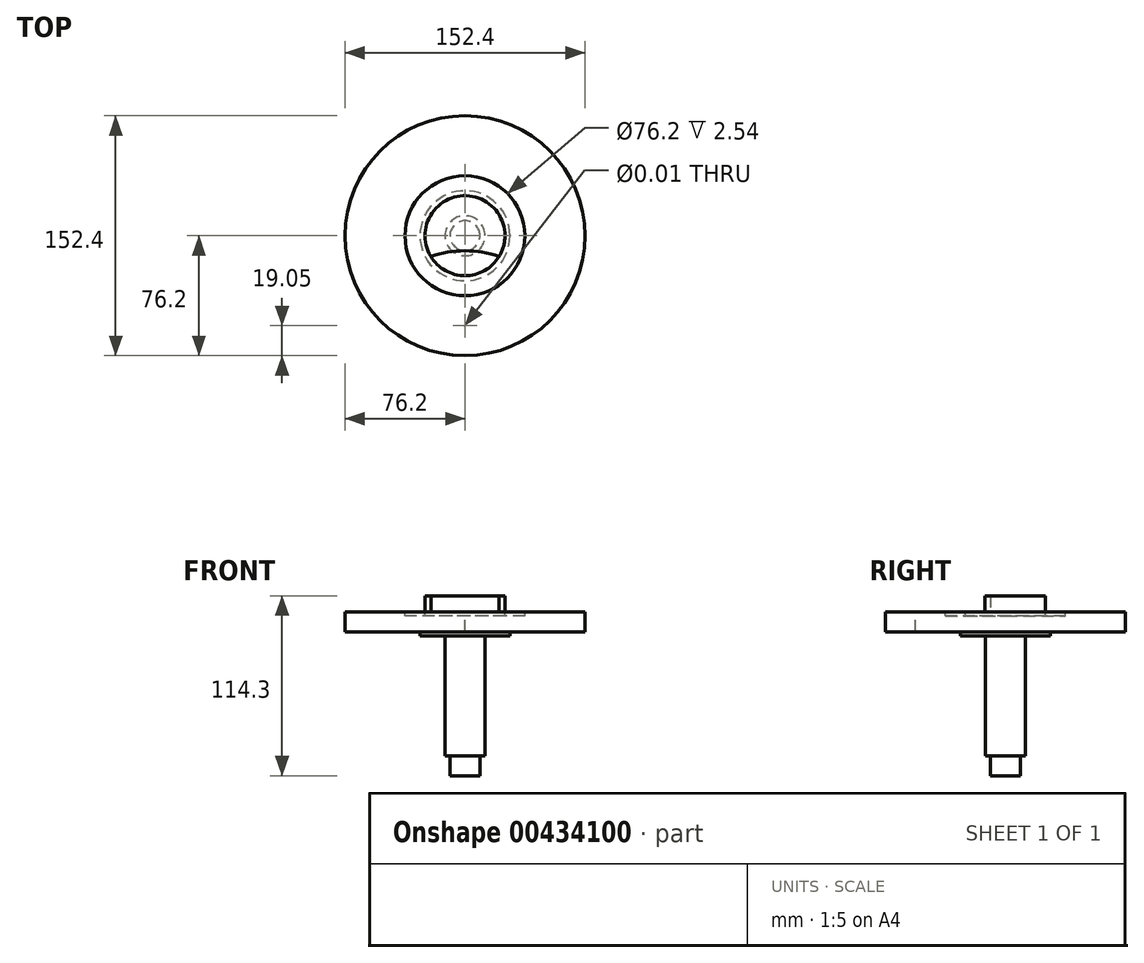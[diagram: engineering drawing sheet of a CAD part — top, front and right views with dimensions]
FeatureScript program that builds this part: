
annotation { "Feature Type Name" : "Feature", "Feature Type Description" : "" }
export const myFeature = defineFeature(function(context is Context, id is Id, definition is map)
    precondition{}
    {
        {
            var Q0;
            Q0=qCreatedBy(makeId("Front.planeOp"),FACE);
            var sketch = newSketch(context, id + "F0", { "sketchPlane" : qUnion([Q0])});
            skLineSegment(sketch, "E0", {"start": v(0, 0) * mm, "end": v(-25.4, 0) * mm});
            skLineSegment(sketch, "E1", {"start": v(-25.4, 0) * mm, "end": v(-25.4, -12.7) * mm});
            skLineSegment(sketch, "E2", {"start": v(-25.4, -12.7) * mm, "end": v(-38.1, -12.7) * mm});
            skLineSegment(sketch, "E3", {"start": v(-38.1, -12.7) * mm, "end": v(-38.1, -10.16) * mm});
            skLineSegment(sketch, "E4", {"start": v(-38.1, -10.16) * mm, "end": v(-76.2, -10.16) * mm});
            skLineSegment(sketch, "E5", {"start": v(-76.2, -10.16) * mm, "end": v(-76.2, -22.86) * mm});
            skLineSegment(sketch, "E6", {"start": v(-76.2, -22.86) * mm, "end": v(-28.58, -22.86) * mm});
            skLineSegment(sketch, "E7", {"start": v(-12.7, -25.4) * mm, "end": v(-12.7, -101.6) * mm});
            skLineSegment(sketch, "E8", {"start": v(-12.7, -101.6) * mm, "end": v(-9.52, -101.6) * mm});
            skLineSegment(sketch, "E9", {"start": v(-9.52, -101.6) * mm, "end": v(-9.52, -114.3) * mm});
            skLineSegment(sketch, "E10", {"start": v(-9.52, -114.3) * mm, "end": v(0, -114.3) * mm});
            skLineSegment(sketch, "E11", {"start": v(0, -114.3) * mm, "end": v(0, 0) * mm});
            skLineSegment(sketch, "E12", {"start": v(-28.58, -22.86) * mm, "end": v(-28.58, -25.4) * mm});
            skLineSegment(sketch, "E13", {"start": v(-28.58, -25.4) * mm, "end": v(-12.7, -25.4) * mm});
            skLineSegment(sketch, "E14", {"start": v(0, 17.27) * mm, "end": v(0, -123.9) * mm, "construction": true});
            skSolve(sketch);
        }
        {
            var Q0;
            Q0=makeQuery(id+"F0.imprint","IMPRINT",FACE,{"disambiguationData":[TD([[makeQuery(id+"F0.imprint","IMPRINT",EDGE,{"derivedFrom":sQuery(id+"F0.wireOp",EDGE,"E0")}),1.0]])]});
            var Q1;
            Q1=sQuery(id+"F0.wireOp",EDGE,"E14");
            var Q2;
            Q2=sQuery(id+"F0.wireOp",EDGE,"E11");
            var Q3;
            Q3=sQuery(id+"F0.wireOp",EDGE,"E0");
            var Q4;
            Q4=sQuery(id+"F0.wireOp",EDGE,"E1");
            var Q5;
            Q5=sQuery(id+"F0.wireOp",EDGE,"E2");
            var Q6;
            Q6=sQuery(id+"F0.wireOp",EDGE,"E3");
            var Q7;
            Q7=sQuery(id+"F0.wireOp",EDGE,"E4");
            var Q8;
            Q8=sQuery(id+"F0.wireOp",EDGE,"E5");
            var Q9;
            Q9=sQuery(id+"F0.wireOp",EDGE,"E6");
            var Q10;
            Q10=sQuery(id+"F0.wireOp",EDGE,"E12");
            var Q11;
            Q11=sQuery(id+"F0.wireOp",EDGE,"E13");
            var Q12;
            Q12=sQuery(id+"F0.wireOp",EDGE,"E7");
            var Q13;
            Q13=sQuery(id+"F0.wireOp",EDGE,"E8");
            var Q14;
            Q14=sQuery(id+"F0.wireOp",EDGE,"E9");
            var Q15;
            Q15=sQuery(id+"F0.wireOp",EDGE,"E10");
            var Q16;
            Q16=sQuery(id+"F0.wireOp",EDGE,"E14");
            revolve(context, id + "F1", {"entities" : qUnion([Q0]), "surfaceEntities" : qUnion([Q1, Q2, Q3, Q4, Q5, Q6, Q7, Q8, Q9, Q10, Q11, Q12, Q13, Q14, Q15]), "axis" : qUnion([Q16]), "revolveType" : RevolveType.FULL});
        }
        {
            var Q0;
            Q0=makeQuery(id+"F1.opRevolve","SWEPT_FACE",FACE,{"disambiguationData":[OSD([sQuery(id+"F0.wireOp",EDGE,"E4")])]});
            var sketch = newSketch(context, id + "F2", { "sketchPlane" : qUnion([Q0])});
            skCircle(sketch, "E15", {"center": v(0, -76.2) * mm, "radius": 66.68 * mm});
            skSolve(sketch);
        }
        {
            var Q0;
            {var subQ0=sQuery(id+"F2.wireOp",EDGE,"E15");var subQ1=makeQuery(id+"F1.opRevolve","SWEPT_EDGE",EDGE,{"disambiguationData":[OSD([sQuery(id+"F0.wireOp",EDGE,"E3"),sQuery(id+"F0.wireOp",EDGE,"E4")])]});var subQ2=makeQuery(id+"F2.imprint","INTERSECT",VERTEX,{"disambiguationData":[OD(0.0)],"derivedFrom":[subQ1,subQ0]});Q0=makeQuery(id+"F2.imprint","IMPRINT",FACE,{"disambiguationData":[TD([[makeQuery(id+"F2.imprint","IMPRINT",EDGE,{"disambiguationData":[TD([[subQ2,-1.0]])],"derivedFrom":subQ0}),1.0]])]});}
            extrude(context, id + "F3", {"entities" : qUnion([Q0]), "operationType" : NewBodyOperationType.REMOVE, "depth" : 25.4 * mm});
        }
        {
            var Q0;
            Q0=makeQuery(id+"F1.opRevolve","SWEPT_FACE",FACE,{"disambiguationData":[OSD([sQuery(id+"F0.wireOp",EDGE,"E4")])]});
            var sketch = newSketch(context, id + "F4", { "sketchPlane" : qUnion([Q0])});
            skLineSegment(sketch, "E16", {"start": v(0, 0) * mm, "end": v(0, -57.15) * mm, "construction": true});
            skPoint(sketch, "E17", {"position": v(0, -57.15) * mm});
            skSolve(sketch);
        }
        {
            var Q0;
            Q0=sQuery(id+"F4.wireOp",VERTEX,"E17");
            var Q1;
            Q1=makeQuery(id+"F1.opRevolve","SWEPT_BODY",BODY,{"disambiguationData":[OSD([sQuery(id+"F0.wireOp",EDGE,"E0"),sQuery(id+"F0.wireOp",EDGE,"E1"),sQuery(id+"F0.wireOp",EDGE,"E2"),sQuery(id+"F0.wireOp",EDGE,"E3"),sQuery(id+"F0.wireOp",EDGE,"E4"),sQuery(id+"F0.wireOp",EDGE,"E5"),sQuery(id+"F0.wireOp",EDGE,"E6"),sQuery(id+"F0.wireOp",EDGE,"E7"),sQuery(id+"F0.wireOp",EDGE,"E8"),sQuery(id+"F0.wireOp",EDGE,"E9"),sQuery(id+"F0.wireOp",EDGE,"E10"),sQuery(id+"F0.wireOp",EDGE,"E11"),sQuery(id+"F0.wireOp",EDGE,"E12"),sQuery(id+"F0.wireOp",EDGE,"E13")])]});
            hole(context, id + "F5", {"style" : HoleStyle.SIMPLE, "endStyle" : HoleEndStyle.THROUGH, "standardTappedOrClearance" : lookupTablePath({ "standard" : "ANSI", "size" : "3/8 (0.38)", "type" : "Drilled" }), "standardBlindInLast" : lookupTablePath({ "standard" : "ANSI", "size" : "3/8", "type" : "Drilled" }), "holeDiameter" : 3 / 203.2 * mm, "tappedDepth" : 8.9 * mm, "tapClearance" : 3, "startFromSketch" : true, "locations" : qUnion([Q0]), "scope" : qUnion([Q1])});
        }
    });
